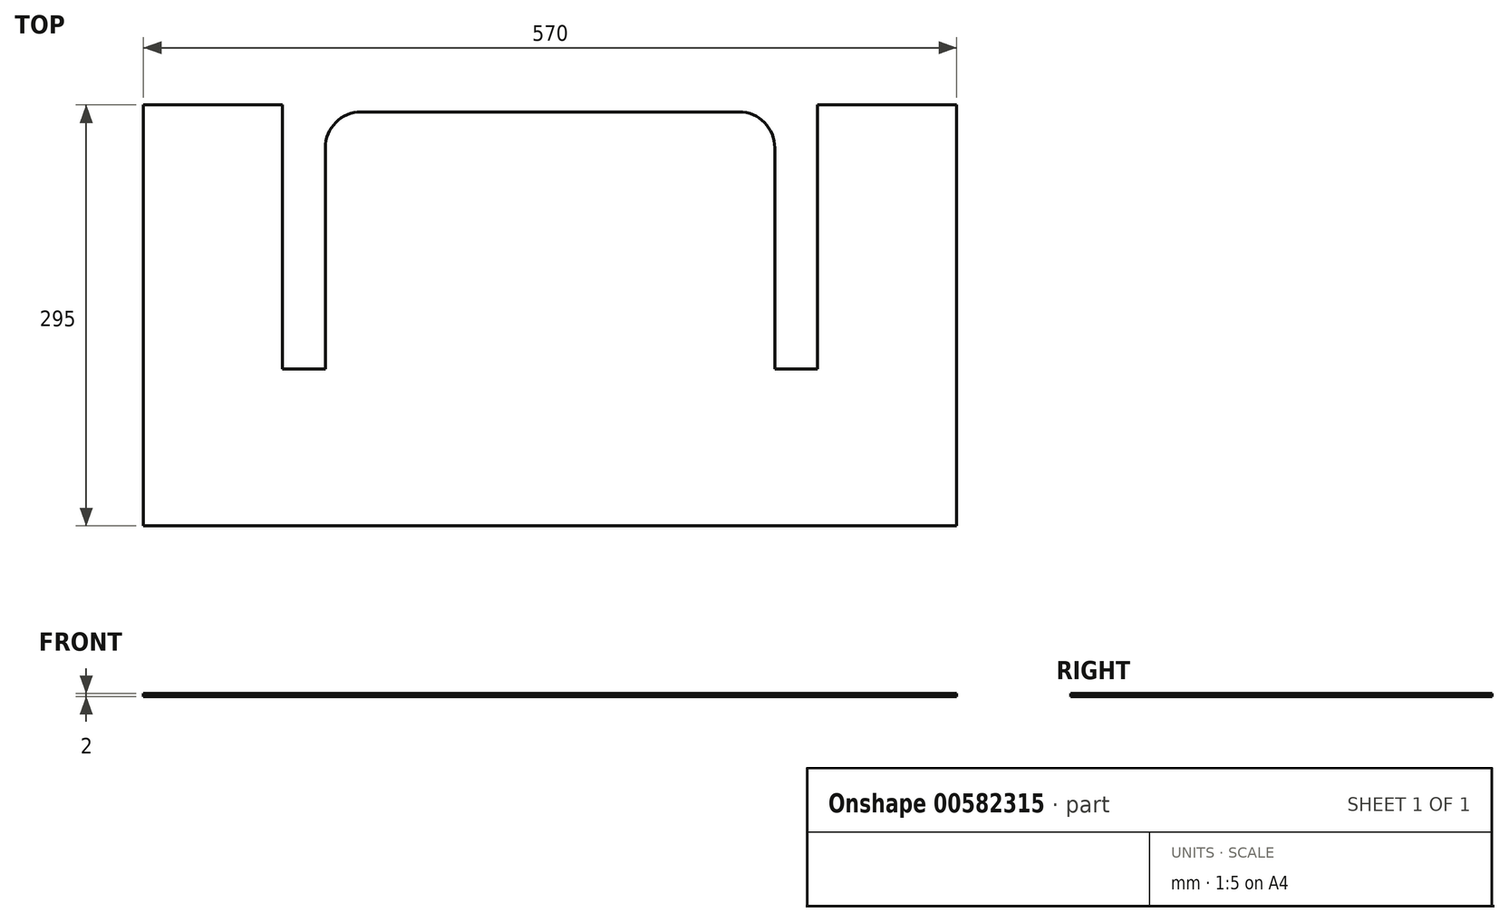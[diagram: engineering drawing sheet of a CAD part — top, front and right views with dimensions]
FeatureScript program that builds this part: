
annotation { "Feature Type Name" : "Feature", "Feature Type Description" : "" }
export const myFeature = defineFeature(function(context is Context, id is Id, definition is map)
    precondition{}
    {
        {
            var Q0;
            Q0=qCreatedBy(makeId("Top.planeOp"),FACE);
            var sketch = newSketch(context, id + "F0", { "sketchPlane" : qUnion([Q0])});
            skLineSegment(sketch, "E0.top", {"start": v(285, -290) * mm, "end": v(-285, -290) * mm});
            skLineSegment(sketch, "E0.left", {"start": v(285, 0) * mm, "end": v(285, -290) * mm});
            skLineSegment(sketch, "E0.right", {"start": v(-285, 0) * mm, "end": v(-285, -290) * mm});
            skPoint(sketch, "E0.middle", {"position": v(0, 0) * mm});
            skPoint(sketch, "E1.orphan", {"position": v(-285, 290) * mm});
            skPoint(sketch, "E2.orphan", {"position": v(285, 290) * mm});
            skLineSegment(sketch, "E3", {"start": v(-187.5, 0) * mm, "end": v(-187.5, -180) * mm});
            skLineSegment(sketch, "E4", {"start": v(-187.5, -180) * mm, "end": v(-157.5, -180) * mm});
            skLineSegment(sketch, "E5", {"start": v(-157.5, -180) * mm, "end": v(-157.5, 0) * mm});
            skLineSegment(sketch, "E6", {"start": v(157.5, 0) * mm, "end": v(157.5, -180) * mm});
            skLineSegment(sketch, "E7", {"start": v(157.5, -180) * mm, "end": v(187.5, -180) * mm});
            skLineSegment(sketch, "E8", {"start": v(187.5, -180) * mm, "end": v(187.5, 0) * mm});
            skLineSegment(sketch, "E9.trimOffspring", {"start": v(-157.5, 0) * mm, "end": v(157.5, 0) * mm});
            skLineSegment(sketch, "E10", {"start": v(187.5, 0) * mm, "end": v(187.5, 5) * mm});
            skLineSegment(sketch, "E11", {"start": v(187.5, 5) * mm, "end": v(285, 5) * mm});
            skLineSegment(sketch, "E12", {"start": v(-285, 0) * mm, "end": v(-285, 5) * mm});
            skLineSegment(sketch, "E13", {"start": v(-285, 5) * mm, "end": v(-187.5, 5) * mm});
            skLineSegment(sketch, "E14", {"start": v(-187.5, 0) * mm, "end": v(-187.5, 5) * mm});
            skPoint(sketch, "E15.orphan", {"position": v(-187.17, 5) * mm});
            skLineSegment(sketch, "E16", {"start": v(285, 0) * mm, "end": v(285, 5) * mm});
            skSolve(sketch);
        }
        {
            var Q0;
            Q0 = qSketchRegion(id + "F0", true);
            extrude(context, id + "F1", {"entities" : qUnion([Q0]), "depth" : 2 * mm, "offsetDistance" : 25 * mm});
        }
        {
            var Q0;
            Q0=makeQuery(id+"F1.opExtrude","SWEPT_EDGE",EDGE,{"disambiguationData":[OSD([sQuery(id+"F0.wireOp",EDGE,"E5"),sQuery(id+"F0.wireOp",EDGE,"E9.trimOffspring")])]});
            var Q1;
            Q1=makeQuery(id+"F1.opExtrude","SWEPT_EDGE",EDGE,{"disambiguationData":[OSD([sQuery(id+"F0.wireOp",EDGE,"E6"),sQuery(id+"F0.wireOp",EDGE,"E9.trimOffspring")])]});
            fillet(context, id + "F2", {"entities" : qUnion([Q0, Q1]), "radius" : 25 * mm, "tangentPropagation" : true, "allowEdgeOverflow" : false});
        }
    });
